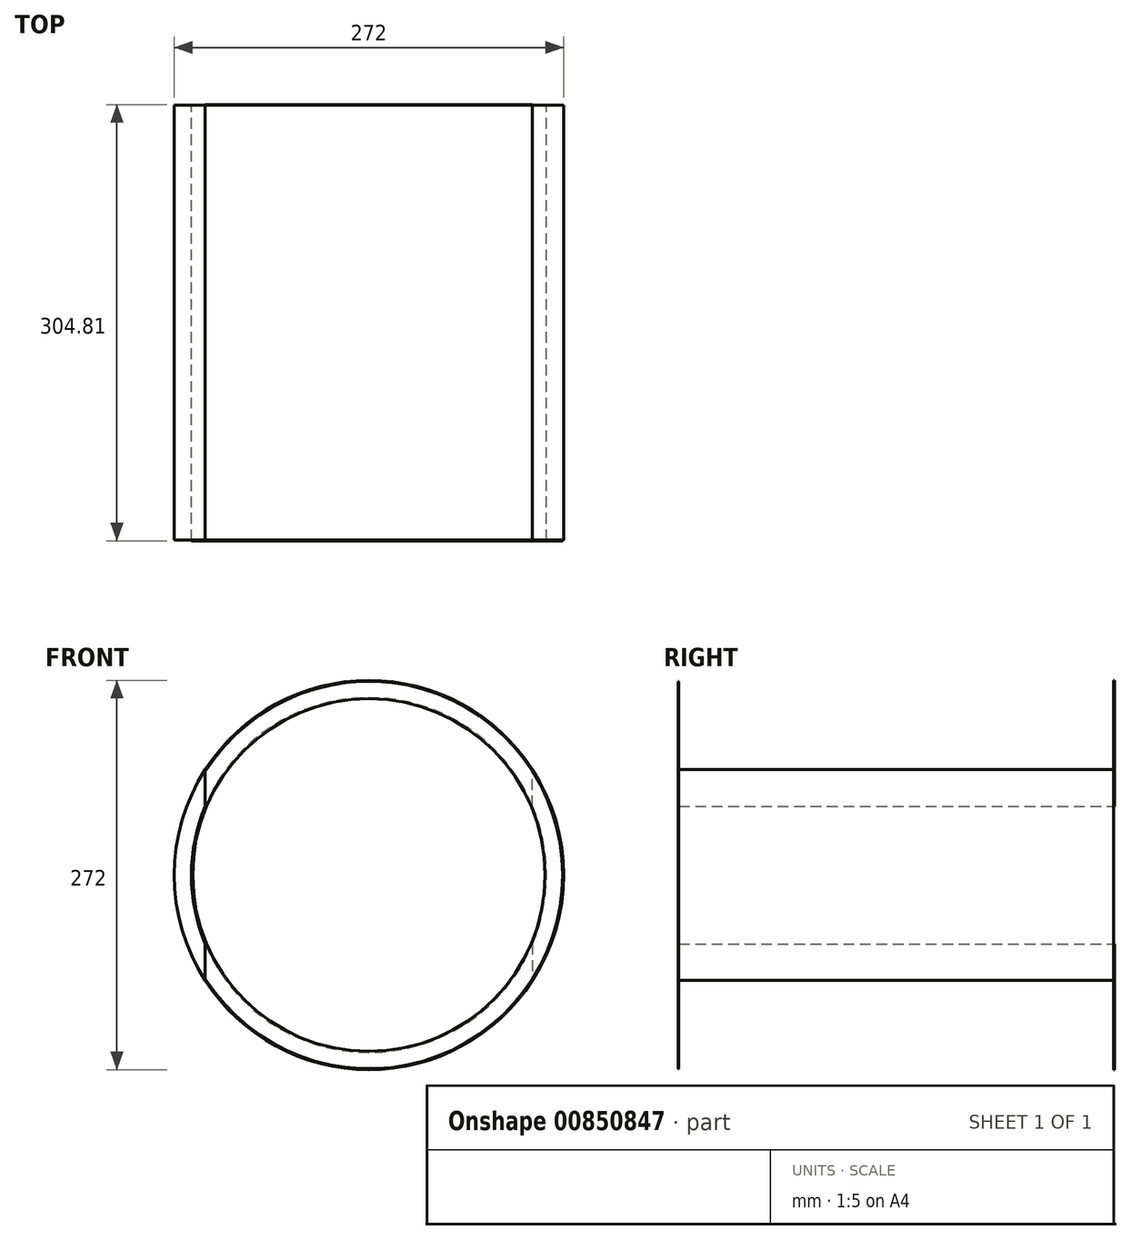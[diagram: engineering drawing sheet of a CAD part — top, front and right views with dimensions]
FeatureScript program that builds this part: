
annotation { "Feature Type Name" : "Feature", "Feature Type Description" : "" }
export const myFeature = defineFeature(function(context is Context, id is Id, definition is map)
    precondition{}
    {
        {
            var Q0;
            Q0=qCreatedBy(makeId("Front.planeOp"),FACE);
            var sketch = newSketch(context, id + "F0", { "sketchPlane" : qUnion([Q0])});
            skCircle(sketch, "E0", {"center": v(-122.55, -161.57) * mm, "radius": 136 * mm});
            skLineSegment(sketch, "E1", {"start": v(-8.25, -113.5) * mm, "end": v(-8.25, -87.87) * mm});
            skLineSegment(sketch, "E2", {"start": v(-8.25, -209.65) * mm, "end": v(-8.25, -235.28) * mm});
            skLineSegment(sketch, "E3", {"start": v(-236.85, -209.65) * mm, "end": v(-236.85, -235.28) * mm});
            skLineSegment(sketch, "E4", {"start": v(-236.85, -113.5) * mm, "end": v(-236.85, -87.86) * mm});
            skCircle(sketch, "E5", {"center": v(-122.55, -161.57) * mm, "radius": 124 * mm});
            skSolve(sketch);
        }
        {
            var Q0;
            {var subQ0=sQuery(id+"F0.wireOp",EDGE,"E4");var subQ1=sQuery(id+"F0.wireOp",EDGE,"E0");var subQ2=makeQuery(id+"F0.imprint","INTERSECT",VERTEX,{"derivedFrom":[subQ1,subQ0]});Q0=makeQuery(id+"F0.imprint","IMPRINT",FACE,{"disambiguationData":[TD([[makeQuery(id+"F0.imprint","IMPRINT",EDGE,{"disambiguationData":[TD([[subQ2,-1.0]])],"derivedFrom":subQ1}),1.0]])]});}
            var Q1;
            {var subQ0=sQuery(id+"F0.wireOp",EDGE,"E1");var subQ1=sQuery(id+"F0.wireOp",EDGE,"E0");var subQ2=makeQuery(id+"F0.imprint","INTERSECT",VERTEX,{"derivedFrom":[subQ1,subQ0]});Q1=makeQuery(id+"F0.imprint","IMPRINT",FACE,{"disambiguationData":[TD([[makeQuery(id+"F0.imprint","IMPRINT",EDGE,{"disambiguationData":[TD([[subQ2,1.0]])],"derivedFrom":subQ1}),1.0]])]});}
            extrude(context, id + "F1", {"entities" : qUnion([Q0, Q1]), "depth" : 303.8 * mm, "offsetDistance" : 25.4 * mm});
        }
        {
            var Q0;
            {var subQ0=sQuery(id+"F0.wireOp",EDGE,"E4");var subQ1=sQuery(id+"F0.wireOp",EDGE,"E0");var subQ2=makeQuery(id+"F0.imprint","INTERSECT",VERTEX,{"derivedFrom":[subQ1,subQ0]});Q0=makeQuery(id+"F0.imprint","IMPRINT",FACE,{"disambiguationData":[TD([[makeQuery(id+"F0.imprint","IMPRINT",EDGE,{"disambiguationData":[TD([[subQ2,1.0]])],"derivedFrom":subQ1}),1.0]])]});}
            var Q1;
            {var subQ0=sQuery(id+"F0.wireOp",EDGE,"E3");var subQ1=sQuery(id+"F0.wireOp",EDGE,"E0");var subQ2=makeQuery(id+"F0.imprint","INTERSECT",VERTEX,{"derivedFrom":[subQ1,subQ0]});Q1=makeQuery(id+"F0.imprint","IMPRINT",FACE,{"disambiguationData":[TD([[makeQuery(id+"F0.imprint","IMPRINT",EDGE,{"disambiguationData":[TD([[subQ2,-1.0]])],"derivedFrom":subQ1}),1.0]])]});}
            extrude(context, id + "F2", {"entities" : qUnion([Q0, Q1]), "oppositeDirection" : true, "depth" : 0.5 * mm, "offsetDistance" : 25.4 * mm});
        }
        {
            var Q0;
            Q0=makeQuery(id+"F1.opExtrude","CAP_FACE",FACE,{"disambiguationData":[OSD([sQuery(id+"F0.wireOp",EDGE,"E0"),sQuery(id+"F0.wireOp",EDGE,"E3"),sQuery(id+"F0.wireOp",EDGE,"E4"),sQuery(id+"F0.wireOp",EDGE,"E5")])],"isStart":false});
            var sketch = newSketch(context, id + "F3", { "sketchPlane" : qUnion([Q0])});
            skCircle(sketch, "E6", {"center": v(-122.55, -161.57) * mm, "radius": 135.35 * mm});
            skCircle(sketch, "E7", {"center": v(-122.55, -161.57) * mm, "radius": 123.14 * mm});
            skSolve(sketch);
        }
        {
            var Q0;
            Q0=makeQuery(id+"F3.imprint","IMPRINT",FACE,{"disambiguationData":[TD([[makeQuery(id+"F3.imprint","IMPRINT",EDGE,{"derivedFrom":sQuery(id+"F3.wireOp",EDGE,"E7")}),-1.0]])]});
            extrude(context, id + "F4", {"entities" : qUnion([Q0]), "operationType" : NewBodyOperationType.ADD, "depth" : 0.5 * mm, "offsetDistance" : 25.4 * mm});
        }
    });
